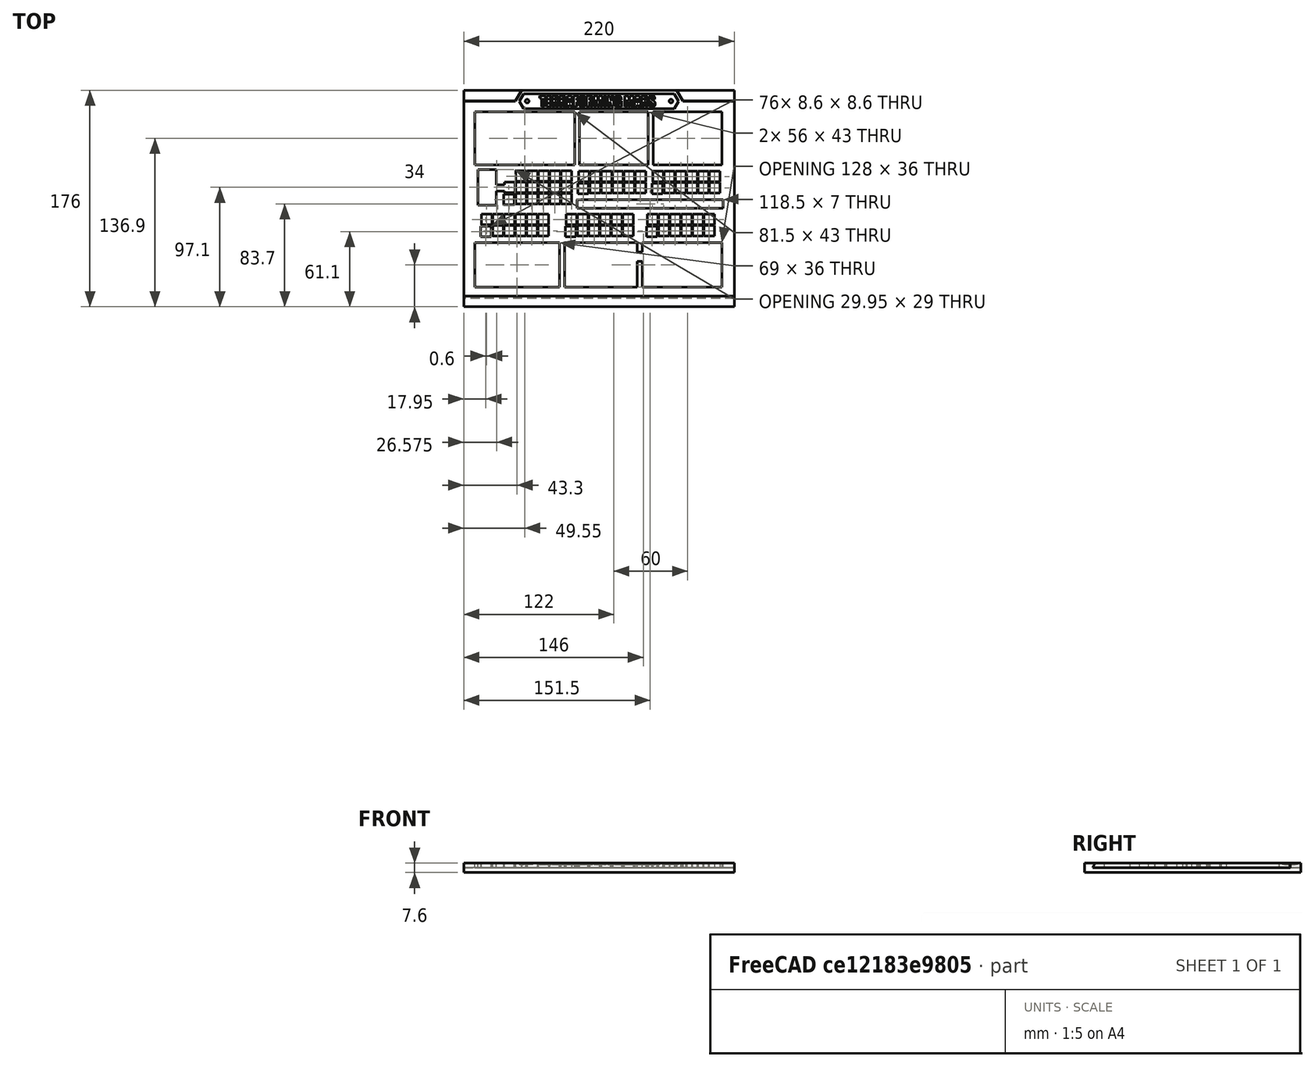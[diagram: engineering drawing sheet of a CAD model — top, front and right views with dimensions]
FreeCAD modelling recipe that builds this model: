
FCSTD DOCUMENT  (FreeCAD 1.0R39109 (Git))
Label: overlay-full-v7-7.6mm-hack
License: All rights reserved
LicenseURL: https://en.wikipedia.org/wiki/All_rights_reserved
objects: Sketcher::SketchObject×10, PartDesign::Pad×9, PartDesign::Pocket×6, Part::Feature×2, PartDesign::Body×2, Mesh::Feature×1, Part::Refine×1, PartDesign::FeatureBase×1, Part::Part2DObjectPython×1, Part::Extrusion×1
note: 74 computed .brp shape members not serialized (recipe doc carries the construction recipe); baked Part::Feature solids carry a one-line shape summary decoded from their .brp

FEATURE [Mesh::Feature] Terraforming_Mars_overlay
FEATURE [Part::Feature] Terraforming_Mars_overlay001
  shape: bbox 208 x 148 x 3.7 mm, 1736 faces, 0 solids (baked)
FEATURE [Part::Feature] Terraforming_Mars_overlay001_solid  label="Terraforming_Mars_overlay001 (Solid)"
  shape: bbox 208 x 148 x 3.7 mm, 1736 faces (baked)
FEATURE [Part::Refine] Terraforming_Mars_overlay001_solid001  label="Terraforming_Mars_overlay001 (Solid)001"
  Source = -> Terraforming_Mars_overlay001_solid
FEATURE [PartDesign::FeatureBase] BaseFeature
  BaseFeature = -> Terraforming_Mars_overlay001_solid001
  Suppressed = false
FEATURE [Sketcher::SketchObject] Sketch
  ArcFitTolerance = 0
  AttachmentSupport = -> [BaseFeature]
  ExternalGeometry = -> [BaseFeature]
  FullyConstrained = true
  MakeInternals = false
  MapMode = 5
  Placement = pos=(0,0,3.7) rot=(0,0,1;0rad)
  sketch-geometry (8):
    g0: LineSegment StartX=6 StartY=154 StartZ=0 EndX=214 EndY=154 EndZ=0
    g1: LineSegment StartX=214 StartY=154 StartZ=0 EndX=214 EndY=6 EndZ=0
    g2: LineSegment StartX=214 StartY=6 StartZ=0 EndX=6 EndY=6 EndZ=0
    g3: LineSegment StartX=6 StartY=6 StartZ=0 EndX=6 EndY=154 EndZ=0
    g4: LineSegment StartX=0 StartY=160 StartZ=0 EndX=220 EndY=160 EndZ=0
    g5: LineSegment StartX=220 StartY=160 StartZ=0 EndX=220 EndY=-0.4 EndZ=0
    g6: LineSegment StartX=220 StartY=-0.4 StartZ=0 EndX=0 EndY=-0.4 EndZ=0
    g7: LineSegment StartX=0 StartY=-0.4 StartZ=0 EndX=0 EndY=160 EndZ=0
  constraints (22):
    c: Coincident(g0,g1)
    c: Coincident(g1,g2)
    c: Coincident(g2,g3)
    c: Coincident(g3,g0)
    c: Horizontal(g0)
    c: Horizontal(g2)
    c: Vertical(g1)
    c: Vertical(g3)
    c: Coincident(g0,g-3)
    c: Coincident(g1,g-4)
    c: Coincident(g4,g5)
    c: Coincident(g5,g6)
    c: Coincident(g6,g7)
    c: Coincident(g7,g4)
    c: Horizontal(g4)
    c: Horizontal(g6)
    c: Vertical(g5)
    c: Vertical(g7)
    c: DistanceX(g4,g0) = 6
    c: DistanceX(g0,g4) = 6
    c: DistanceY(g0,g4) = 6
    c: DistanceY(g5,g1) = 6.4
FEATURE [PartDesign::Pad] Pad
  BaseFeature = -> BaseFeature
  Direction = (0,0,1)
  Length = 10
  Length2 = 10
  Profile = -> Sketch
  ReferenceAxis = -> Sketch [N_Axis]
  Suppressed = false
  Type = 3
  UpToFace = -> BaseFeature [Face1]
FEATURE [Sketcher::SketchObject] Sketch001
  ArcFitTolerance = 0
  AttachmentSupport = -> [Pad]
  ExternalGeometry = -> [Pad]
  FullyConstrained = true
  MakeInternals = false
  MapMode = 5
  Placement = pos=(0,0,3.7) rot=(0,0,1;0rad)
  sketch-geometry (5):
    g0: GeomPoint [constr] X=110 Y=160 Z=0
    g1: LineSegment StartX=42 StartY=160 StartZ=0 EndX=47.0807 EndY=168.8 EndZ=0
    g2: LineSegment StartX=47.0807 StartY=168.8 StartZ=0 EndX=172.919 EndY=168.8 EndZ=0
    g3: LineSegment StartX=172.919 StartY=168.8 StartZ=0 EndX=178 EndY=160 EndZ=0
    g4: LineSegment StartX=178 StartY=160 StartZ=0 EndX=42 EndY=160 EndZ=0
  constraints (13):
    c: Symmetric(g-3,g-3,g0)
    c: Coincident(g1,g2)
    c: Horizontal(g2)
    c: Coincident(g2,g3)
    c: Coincident(g3,g4)
    c: Coincident(g4,g1)
    c: Angle(g1,g4,g1) = 2.0944
    c: Angle(g4,g3,g3) = 2.0944
    c: DistanceY(g1,g1) = 8.8
    c: PointOnObject(g1,g-3)
    c: DistanceX(g-3,g1) = 42
    c: DistanceX(g3,g-3) = 42
    c: PointOnObject(g3,g-3)
FEATURE [PartDesign::Pad] Pad001
  BaseFeature = -> Pad
  Direction = (0,0,1)
  Length = 10
  Length2 = 10
  Profile = -> Sketch001
  ReferenceAxis = -> Sketch001 [N_Axis]
  Suppressed = false
  Type = 3
  UpToFace = -> Pad [Face2]
FEATURE [Sketcher::SketchObject] Sketch002
  ArcFitTolerance = 0
  AttachmentSupport = -> [Pad001]
  ExternalGeometry = -> [Pad001]
  FullyConstrained = true
  MakeInternals = false
  MapMode = 5
  Placement = pos=(0,0,3.7) rot=(0,0,1;0rad)
  sketch-geometry (7):
    g0: GeomPoint [constr] X=110 Y=160 Z=0
    g1: LineSegment StartX=45.2332 StartY=160 StartZ=0 EndX=48.6973 EndY=166 EndZ=0
    g2: LineSegment StartX=48.6973 StartY=166 StartZ=0 EndX=171.303 EndY=166 EndZ=0
    g3: LineSegment StartX=171.303 StartY=166 StartZ=0 EndX=174.767 EndY=160 EndZ=0
    g4: LineSegment StartX=174.767 StartY=160 StartZ=0 EndX=171.303 EndY=154 EndZ=0
    g5: LineSegment StartX=171.303 StartY=154 StartZ=0 EndX=48.6973 EndY=154 EndZ=0
    g6: LineSegment StartX=48.6973 StartY=154 StartZ=0 EndX=45.2332 EndY=160 EndZ=0
  constraints (17):
    c: Symmetric(g-4,g-4,g0)
    c: PointOnObject(g1,g-4)
    c: Coincident(g1,g2)
    c: Horizontal(g2)
    c: Coincident(g2,g3)
    c: PointOnObject(g3,g-4)
    c: Coincident(g3,g4)
    c: PointOnObject(g4,g-5)
    c: Coincident(g4,g5)
    c: Coincident(g5,g6)
    c: Coincident(g6,g1)
    c: Parallel(g1,g-6)
    c: Symmetric(g5,g1,g-4)
    c: Symmetric(g4,g2,g-4)
    c: Parallel(g3,g-7)
    c: Distance(g1,g-6) = 2.8
    c: Distance(g2,g-7) = 2.8
FEATURE [PartDesign::Pocket] Pocket
  BaseFeature = -> Pad001
  Direction = (0,0,-1)
  Length = 1.1
  Length2 = 5
  Profile = -> Sketch002
  ReferenceAxis = -> Sketch002 [N_Axis]
  Suppressed = false
  Type = 0
FEATURE [Part::Part2DObjectPython] ShapeString  # Draft 2D object (typed FeaturePython)
  FontFile = <path>
  Fuse = false
  Justification = 6
  JustificationReference = 0
  KeepLeftMargin = true
  MakeFace = true
  ObliqueAngle = 0
  Placement = pos=(61.7,155.5,2.7) rot=(0,0,1;0rad)
  ScaleToSize = false
  Size = 9
  String = TERRAFORMING MARS
  Tracking = 0
FEATURE [Sketcher::SketchObject] Sketch003
  ArcFitTolerance = 0
  AttachmentSupport = -> [Pocket]
  ExternalGeometry = -> [Pocket]
  FullyConstrained = true
  MakeInternals = false
  MapMode = 5
  Placement = pos=(0,0,2.6) rot=(0,0,1;0rad)
  sketch-geometry (3):
    g0: LineSegment [constr] StartX=42 StartY=160 StartZ=0 EndX=178 EndY=160 EndZ=0
    g1: Circle CenterX=51.5 CenterY=160 CenterZ=0 NormalX=0 NormalY=0 NormalZ=1 AngleXU=0 Radius=1.5
    g2: Circle CenterX=168.5 CenterY=160 CenterZ=0 NormalX=0 NormalY=0 NormalZ=1 AngleXU=0 Radius=1.5
  constraints (8):
    c: Coincident(g0,g-3)
    c: Coincident(g0,g-4)
    c: PointOnObject(g1,g0)
    c: PointOnObject(g2,g0)
    c: Diameter(g2) = 3
    c: Diameter(g1) = 3
    c: DistanceX(g0,g1) = 9.5
    c: DistanceX(g2,g0) = 9.5
FEATURE [PartDesign::Pad] Pad002
  BaseFeature = -> Pocket
  Direction = (0,0,1)
  Length = 1
  Length2 = 10
  Profile = -> Sketch003
  ReferenceAxis = -> Sketch003 [N_Axis]
  Suppressed = false
  Type = 0
FEATURE [Part::Extrusion] Extrude  label="Text"
  Base = -> ShapeString
  Dir = (0,0,1)
  DirMode = 2
  FaceMakerClass = Part::FaceMakerBullseye
  FaceMakerMode = 3
  LengthFwd = 1
  LengthRev = 0
  Placement = pos=(0,0.4,-0.1) rot=(0,0,1;0rad)
  Solid = false
  Symmetric = false
FEATURE [Sketcher::SketchObject] Sketch005
  ArcFitTolerance = 0
  AttachmentSupport = -> [XY_Plane001]
  FullyConstrained = true
  MakeInternals = false
  MapMode = 5
  sketch-geometry (4):
    g0: LineSegment StartX=0 StartY=160.4 StartZ=0 EndX=220 EndY=160.4 EndZ=0
    g1: LineSegment StartX=220 StartY=160.4 StartZ=0 EndX=220 EndY=0 EndZ=0
    g2: LineSegment StartX=220 StartY=0 StartZ=0 EndX=0 EndY=0 EndZ=0
    g3: LineSegment StartX=0 StartY=0 StartZ=0 EndX=0 EndY=160.4 EndZ=0
  constraints (12):
    c: Coincident(g0,g1)
    c: Coincident(g1,g2)
    c: Coincident(g2,g3)
    c: Coincident(g3,g0)
    c: Horizontal(g0)
    c: Horizontal(g2)
    c: Vertical(g1)
    c: Vertical(g3)
    c: PointOnObject(g1,g-1)
    c: PointOnObject(g0,g-2)
    c: DistanceX(g0,g0) = 220
    c: DistanceY(g1,g1) = 160.4
FEATURE [PartDesign::Pad] Pad004
  Direction = (0,0,1)
  Length = 4
  Length2 = 10
  Profile = -> Sketch005
  ReferenceAxis = -> Sketch005 [N_Axis]
  Reversed = true
  Suppressed = false
  Type = 0
FEATURE [PartDesign::Pad] Pad005
  BaseFeature = -> Pad004
  Direction = (0,-1,0)
  Length = 6.8
  Length2 = 10
  Profile = -> Pad004 [Face3]
  Suppressed = false
  Type = 0
FEATURE [PartDesign::Pad] Pad006
  BaseFeature = -> Pad005
  Direction = (0,0,1)
  Length = 3.6
  Length2 = 10
  Profile = -> Pad005 [Face8]
  Suppressed = false
  Type = 0
FEATURE [PartDesign::Pad] Pad007
  BaseFeature = -> Pad006
  Direction = (0,1,0)
  Length = 2
  Length2 = 10
  Profile = -> Pad006 [Face8]
  Suppressed = false
  Type = 0
FEATURE [Sketcher::SketchObject] Sketch006
  ArcFitTolerance = 0
  AttachmentSupport = -> [Pad007]
  ExternalGeometry = -> [Pad007]
  FullyConstrained = true
  MakeInternals = false
  MapMode = 5
  Placement = pos=(220,0,0) rot=(0.57735,0.57735,0.57735;2.0944rad)
  sketch-geometry (4):
    g0: LineSegment StartX=-0.1 StartY=0 StartZ=0 EndX=2 EndY=0 EndZ=0
    g1: LineSegment StartX=2 StartY=0 StartZ=0 EndX=2 EndY=3.6 EndZ=0
    g2: LineSegment StartX=-0.1 StartY=0 StartZ=0 EndX=1.9 EndY=3.6 EndZ=0
    g3: LineSegment StartX=1.9 StartY=3.6 StartZ=0 EndX=2 EndY=3.6 EndZ=0
  constraints (10):
    c: PointOnObject(g0,g-1)
    c: Coincident(g0,g-5)
    c: Coincident(g1,g0)
    c: DistanceX(g0,g0) = 2.1
    c: Coincident(g2,g0)
    c: PointOnObject(g2,g-4)
    c: Coincident(g3,g2)
    c: Coincident(g3,g1)
    c: DistanceX(g3,g3) = 0.1
    c: Coincident(g1,g-5)
FEATURE [PartDesign::Pocket] Pocket002
  BaseFeature = -> Pad007
  Direction = (-1,0,0)
  Length = 5
  Length2 = 5
  Profile = -> Sketch006
  ReferenceAxis = -> Sketch006 [N_Axis]
  Suppressed = false
  Type = 1
FEATURE [PartDesign::Pad] Pad008
  BaseFeature = -> Pocket002
  Direction = (0,1,0)
  Length = 8.8
  Length2 = 10
  Profile = -> Pocket002 [Face1]
  Suppressed = false
  Type = 0
FEATURE [Sketcher::SketchObject] Sketch007
  ArcFitTolerance = 0
  AttachmentSupport = -> [Pad008]
  ExternalGeometry = -> [Pad008]
  FullyConstrained = true
  MakeInternals = false
  MapMode = 5
  sketch-geometry (12):
    g0: LineSegment [constr] StartX=47.0807 StartY=169.2 StartZ=0 EndX=42 EndY=160.4 EndZ=0
    g1: LineSegment [constr] StartX=42 StartY=160.4 StartZ=0 EndX=0 EndY=160.4 EndZ=0
    g2: LineSegment StartX=0 StartY=169.2 StartZ=0 EndX=0 EndY=160.5 EndZ=0
    g3: LineSegment StartX=0 StartY=160.5 StartZ=0 EndX=41.9423 EndY=160.5 EndZ=0
    g4: LineSegment StartX=41.9423 StartY=160.5 StartZ=0 EndX=46.9652 EndY=169.2 EndZ=0
    g5: LineSegment StartX=46.9652 StartY=169.2 StartZ=0 EndX=0 EndY=169.2 EndZ=0
    g6: LineSegment [constr] StartX=220 StartY=160.4 StartZ=0 EndX=178 EndY=160.4 EndZ=0
    g7: LineSegment [constr] StartX=172.919 StartY=169.2 StartZ=0 EndX=178 EndY=160.4 EndZ=0
    g8: LineSegment StartX=173.035 StartY=169.2 StartZ=0 EndX=220 EndY=169.2 EndZ=0
    g9: LineSegment StartX=220 StartY=169.2 StartZ=0 EndX=220 EndY=160.5 EndZ=0
    g10: LineSegment StartX=220 StartY=160.5 StartZ=0 EndX=178.058 EndY=160.5 EndZ=0
    g11: LineSegment StartX=178.058 StartY=160.5 StartZ=0 EndX=173.035 EndY=169.2 EndZ=0
  constraints (34):
    c: PointOnObject(g0,g-4)
    c: PointOnObject(g0,g-3)
    c: Coincident(g0,g1)
    c: Coincident(g1,g-3)
    c: DistanceX(g1,g1) = 42
    c: Angle(g0,g-3,g0) = 2.0944
    c: Coincident(g-4,g2)
    c: PointOnObject(g2,g-2)
    c: Coincident(g2,g3)
    c: Horizontal(g3)
    c: Coincident(g3,g4)
    c: PointOnObject(g4,g-4)
    c: Coincident(g4,g5)
    c: Coincident(g5,g2)
    c: Distance(g2,g1) = 0.1
    c: Distance(g4,g0) = 0.1
    c: Parallel(g4,g0)
    c: Coincident(g6,g-3)
    c: PointOnObject(g6,g-3)
    c: PointOnObject(g7,g-4)
    c: Coincident(g7,g6)
    c: DistanceX(g6,g6) = 42
    c: Angle(g7,g-3,g6) = 1.0472
    c: PointOnObject(g8,g-4)
    c: Coincident(g8,g-4)
    c: Coincident(g8,g9)
    c: Vertical(g9)
    c: Coincident(g9,g10)
    c: Horizontal(g10)
    c: Coincident(g10,g11)
    c: Coincident(g11,g8)
    c: Distance(g9,g6) = 0.1
    c: Distance(g8,g7) = 0.1
    c: Parallel(g11,g7)
FEATURE [PartDesign::Pad] Pad009
  BaseFeature = -> Pad008
  Direction = (0,0,1)
  Length = 3.6
  Length2 = 10
  Profile = -> Sketch007
  ReferenceAxis = -> Sketch007 [N_Axis]
  Suppressed = false
  Type = 0
FEATURE [Sketcher::SketchObject] Sketch008
  ArcFitTolerance = 0
  AttachmentSupport = -> [Pad009]
  ExternalGeometry = -> [Pad009]
  FullyConstrained = true
  MakeInternals = false
  MapMode = 5
  sketch-geometry (4):
    g0: LineSegment StartX=0 StartY=0 StartZ=0 EndX=220 EndY=0 EndZ=0
    g1: LineSegment StartX=220 StartY=0 StartZ=0 EndX=220 EndY=160.4 EndZ=0
    g2: LineSegment StartX=220 StartY=160.4 StartZ=0 EndX=0 EndY=160.4 EndZ=0
    g3: LineSegment StartX=0 StartY=160.4 StartZ=0 EndX=0 EndY=0 EndZ=0
  constraints (10):
    c: Coincident(g0,g1)
    c: Coincident(g1,g2)
    c: Coincident(g2,g3)
    c: Coincident(g3,g0)
    c: Horizontal(g0)
    c: Horizontal(g2)
    c: Vertical(g1)
    c: Vertical(g3)
    c: Coincident(g0,g-1)
    c: Coincident(g1,g-3)
FEATURE [PartDesign::Pocket] Pocket003
  BaseFeature = -> Pad009
  Direction = (0,0,-1)
  Length = 0.2
  Length2 = 5
  Profile = -> Sketch008
  ReferenceAxis = -> Sketch008 [N_Axis]
  Suppressed = false
  Type = 0
FEATURE [Sketcher::SketchObject] Sketch009
  ArcFitTolerance = 0
  AttachmentSupport = -> [Pad002]
  ExternalGeometry = -> [Pad002]
  FullyConstrained = true
  MakeInternals = false
  MapMode = 5
  Placement = pos=(220,0,0) rot=(0.57735,0.57735,0.57735;2.0944rad)
  sketch-geometry (3):
    g0: LineSegment StartX=1.6 StartY=3.7 StartZ=0 EndX=-0.4 EndY=0 EndZ=0
    g1: LineSegment StartX=1.6 StartY=3.7 StartZ=0 EndX=-0.4 EndY=3.7 EndZ=0
    g2: LineSegment StartX=-0.4 StartY=3.7 StartZ=0 EndX=-0.4 EndY=0 EndZ=0
  constraints (8):
    c: PointOnObject(g0,g-3)
    c: Coincident(g1,g0)
    c: Coincident(g1,g-4)
    c: Coincident(g2,g1)
    c: Coincident(g2,g0)
    c: Vertical(g2)
    c: DistanceX(g1,g1) = 2
    c: PointOnObject(g0,g-1)
FEATURE [PartDesign::Pocket] Pocket004
  BaseFeature = -> Pad002
  Direction = (-1,0,0)
  Length = 5
  Length2 = 5
  Profile = -> Sketch009
  ReferenceAxis = -> Sketch009 [N_Axis]
  Suppressed = false
  Type = 1
FEATURE [Sketcher::SketchObject] Sketch010
  ArcFitTolerance = 0
  AttachmentSupport = -> [Pocket004]
  ExternalGeometry = -> [Pocket004]
  FullyConstrained = true
  MakeInternals = false
  MapMode = 5
  Placement = pos=(0,0,3.7) rot=(0,0,1;0rad)
  sketch-geometry (4):
    g0: LineSegment StartX=0 StartY=0 StartZ=0 EndX=220 EndY=0 EndZ=0
    g1: LineSegment StartX=220 StartY=0 StartZ=0 EndX=220 EndY=168.8 EndZ=0
    g2: LineSegment StartX=220 StartY=168.8 StartZ=0 EndX=0 EndY=168.8 EndZ=0
    g3: LineSegment StartX=0 StartY=168.8 StartZ=0 EndX=0 EndY=0 EndZ=0
  constraints (11):
    c: Coincident(g0,g1)
    c: Coincident(g1,g2)
    c: Coincident(g2,g3)
    c: Coincident(g3,g0)
    c: Horizontal(g0)
    c: Horizontal(g2)
    c: Vertical(g1)
    c: Vertical(g3)
    c: Coincident(g0,g-1)
    c: PointOnObject(g-3,g2)
    c: PointOnObject(g-4,g1)
FEATURE [PartDesign::Pocket] Pocket005
  BaseFeature = -> Pocket004
  Direction = (0,0,-1)
  Length = 0.1
  Length2 = 5
  Profile = -> Sketch010
  ReferenceAxis = -> Sketch010 [N_Axis]
  Suppressed = false
  Type = 0
FEATURE [PartDesign::Body] Body  label="Front"
  AllowCompound = false
  BaseFeature = -> Terraforming_Mars_overlay001_solid001
  Group = -> [BaseFeature,Sketch,Pad,Sketch001,Pad001,Sketch002,Pocket,Sketch003,Pad002,Sketch009,Pocket004,Sketch010,Pocket005]
  Origin = -> Origin
  Placement = pos=(0,0.4,0) rot=(0,0,1;0rad)
  Tip = -> Pocket005
FEATURE [PartDesign::Pocket] Pocket006
  BaseFeature = -> Pocket003
  Direction = (0,0,-1)
  Length = 0
  Length2 = 5
  Profile = -> Pocket003 [Face2]
  Refine = true
  Suppressed = false
  Type = 3
  UpToFace = -> Pocket003 [Face16]
FEATURE [PartDesign::Body] Body001  label="Back"
  AllowCompound = false
  Group = -> [Sketch005,Pad004,Pad005,Pad006,Pad007,Sketch006,Pocket002,Pad008,Sketch007,Pad009,Sketch008,Pocket003,Pocket006]
  Origin = -> Origin001
  Tip = -> Pocket006
note: 1 file-system path scrubbed to <path> (originals preserved in the JSON sidecar)
